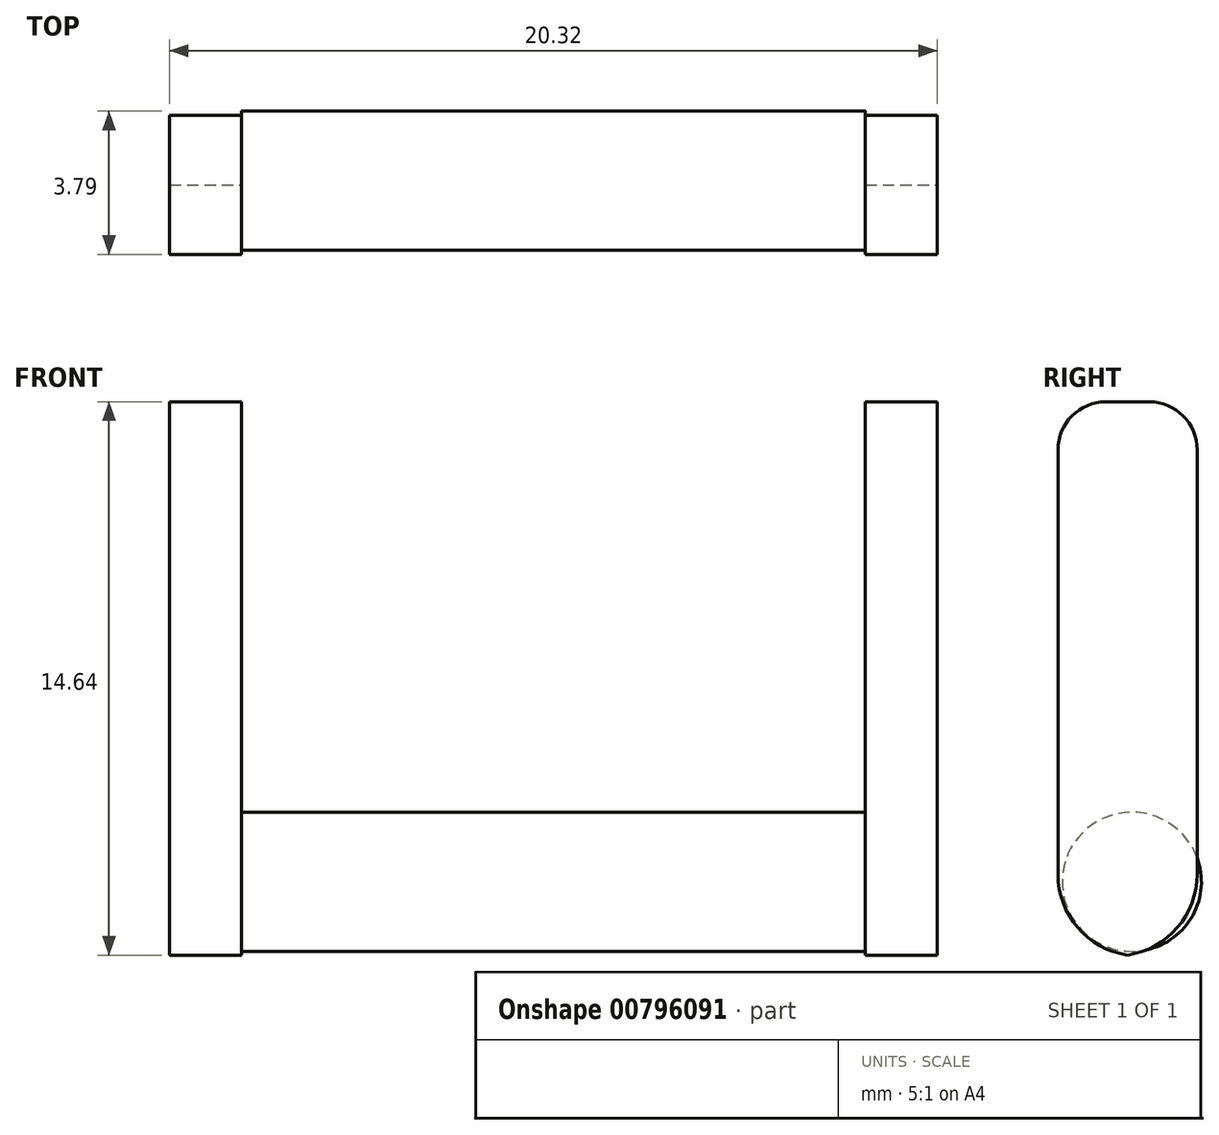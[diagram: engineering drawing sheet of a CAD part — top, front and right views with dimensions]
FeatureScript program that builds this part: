
annotation { "Feature Type Name" : "Feature", "Feature Type Description" : "" }
export const myFeature = defineFeature(function(context is Context, id is Id, definition is map)
    precondition{}
    {
        {
            var Q0;
            Q0=qCreatedBy(makeId("Right.planeOp"),FACE);
            var sketch = newSketch(context, id + "F0", { "sketchPlane" : qUnion([Q0])});
            skCircle(sketch, "E0", {"center": v(0, 0) * mm, "radius": 1.84 * mm});
            skSolve(sketch);
        }
        {
            var Q0;
            Q0 = qSketchRegion(id + "F0", true);
            extrude(context, id + "F1", {"entities" : qUnion([Q0]), "depth" : 16.5 * mm, "offsetDistance" : 25.4 * mm});
        }
        {
            var Q0;
            Q0=qCreatedBy(makeId("Top.planeOp"),FACE);
            var sketch = newSketch(context, id + "F2", { "sketchPlane" : qUnion([Q0])});
            skLineSegment(sketch, "E1.bottom", {"start": v(16.51, 1.73) * mm, "end": v(18.42, 1.73) * mm});
            skLineSegment(sketch, "E1.top", {"start": v(16.51, -1.95) * mm, "end": v(18.42, -1.95) * mm});
            skLineSegment(sketch, "E1.left", {"start": v(16.51, 1.73) * mm, "end": v(16.51, -1.95) * mm});
            skLineSegment(sketch, "E1.right", {"start": v(18.42, 1.73) * mm, "end": v(18.42, -1.95) * mm});
            skLineSegment(sketch, "E2.bottom", {"start": v(-1.9, 1.73) * mm, "end": v(0, 1.73) * mm});
            skLineSegment(sketch, "E2.top", {"start": v(-1.9, -1.95) * mm, "end": v(0, -1.95) * mm});
            skLineSegment(sketch, "E2.left", {"start": v(-1.9, 1.73) * mm, "end": v(-1.9, -1.95) * mm});
            skLineSegment(sketch, "E2.right", {"start": v(0, 1.73) * mm, "end": v(0, -1.95) * mm});
            skSolve(sketch);
        }
        {
            var Q0;
            Q0 = qSketchRegion(id + "F2", true);
            extrude(context, id + "F3", {"entities" : qUnion([Q0]), "operationType" : NewBodyOperationType.ADD, "depth" : 12.7 * mm, "offsetDistance" : 25.4 * mm, "hasSecondDirection" : true, "secondDirectionOppositeDirection" : true, "secondDirectionDepth" : 1.96 * mm});
        }
        {
            var Q0;
            Q0=makeQuery(id+"F3.opExtrude","CAP_EDGE",EDGE,{"disambiguationData":[OSD([sQuery(id+"F2.wireOp",EDGE,"E1.top")])],"isStart":true});
            var Q1;
            Q1=makeQuery(id+"F3.opExtrude","CAP_EDGE",EDGE,{"disambiguationData":[OSD([sQuery(id+"F2.wireOp",EDGE,"E1.bottom")])],"isStart":true});
            var Q2;
            Q2=makeQuery(id+"F3.opExtrude","CAP_EDGE",EDGE,{"disambiguationData":[OSD([sQuery(id+"F2.wireOp",EDGE,"E2.top")])],"isStart":true});
            var Q3;
            Q3=makeQuery(id+"F3.opExtrude","CAP_EDGE",EDGE,{"disambiguationData":[OSD([sQuery(id+"F2.wireOp",EDGE,"E2.bottom")])],"isStart":true});
            fillet(context, id + "F4", {"entities" : qUnion([Q0, Q1, Q2, Q3]), "radius" : 2.16 * mm, "tangentPropagation" : true, "allowEdgeOverflow" : false});
        }
        {
            var Q0;
            Q0=makeQuery(id+"F3.opExtrude","CAP_EDGE",EDGE,{"disambiguationData":[OSD([sQuery(id+"F2.wireOp",EDGE,"E2.top")])],"isStart":false});
            var Q1;
            Q1=makeQuery(id+"F3.opExtrude","CAP_EDGE",EDGE,{"disambiguationData":[OSD([sQuery(id+"F2.wireOp",EDGE,"E2.bottom")])],"isStart":false});
            var Q2;
            Q2=makeQuery(id+"F3.opExtrude","CAP_EDGE",EDGE,{"disambiguationData":[OSD([sQuery(id+"F2.wireOp",EDGE,"E1.bottom")])],"isStart":false});
            var Q3;
            Q3=makeQuery(id+"F3.opExtrude","CAP_EDGE",EDGE,{"disambiguationData":[OSD([sQuery(id+"F2.wireOp",EDGE,"E1.top")])],"isStart":false});
            fillet(context, id + "F5", {"entities" : qUnion([Q0, Q1, Q2, Q3]), "radius" : 1.27 * mm, "tangentPropagation" : true, "allowEdgeOverflow" : false});
        }
    });
